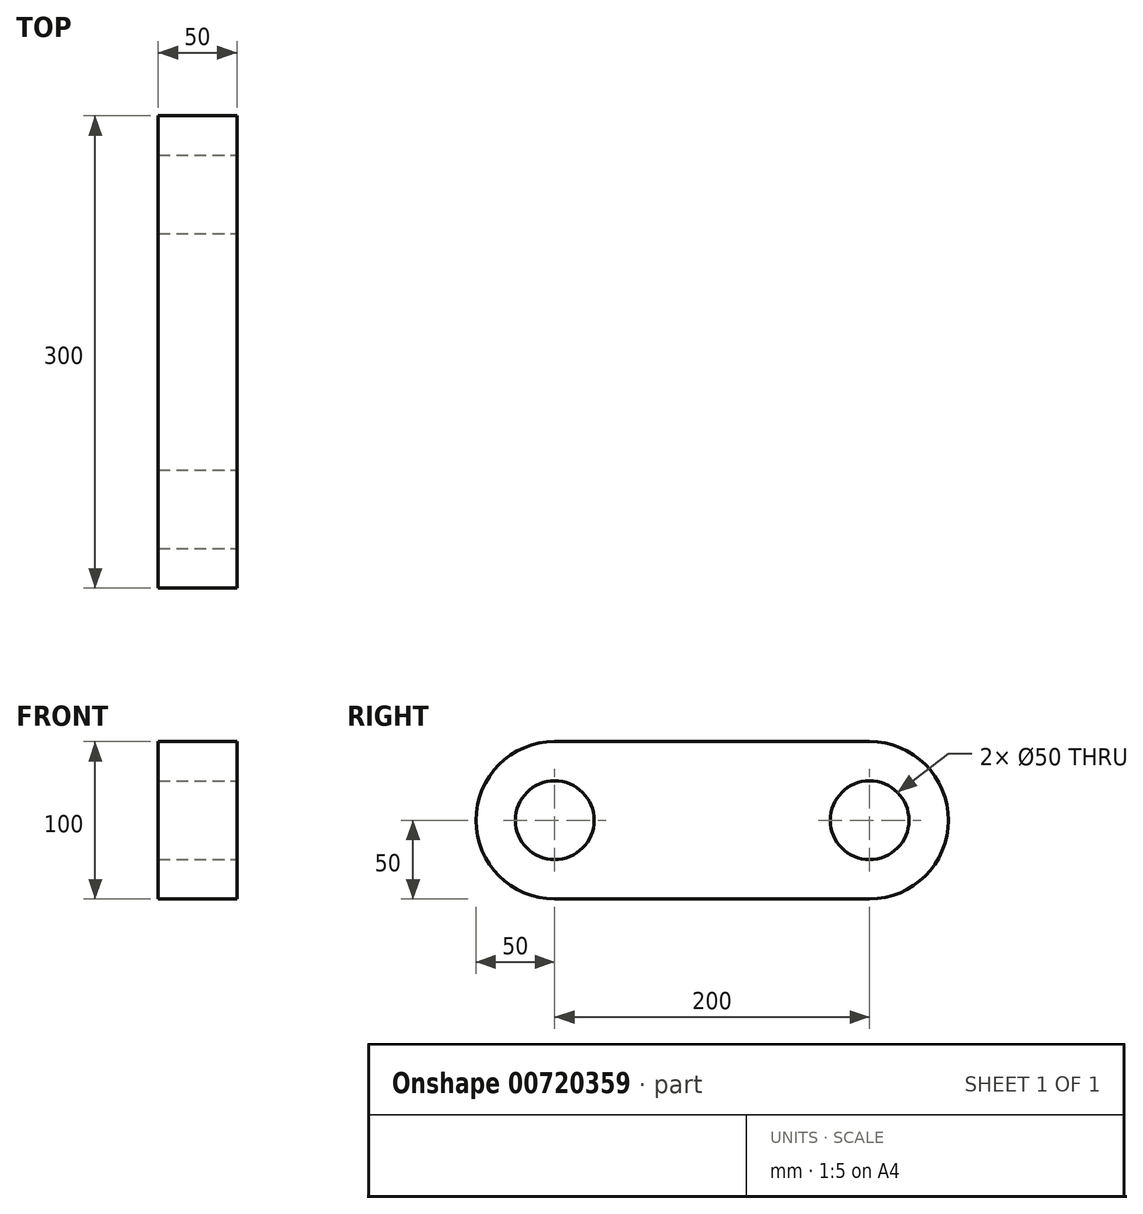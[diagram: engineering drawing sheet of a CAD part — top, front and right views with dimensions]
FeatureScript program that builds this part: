
annotation { "Feature Type Name" : "Feature", "Feature Type Description" : "" }
export const myFeature = defineFeature(function(context is Context, id is Id, definition is map)
    precondition{}
    {
        {
            var Q0;
            Q0=qCreatedBy(makeId("Right.planeOp"),FACE);
            var sketch = newSketch(context, id + "F0", { "sketchPlane" : qUnion([Q0])});
            skLineSegment(sketch, "E0.bottom", {"start": v(150, 50) * mm, "end": v(-150, 50) * mm});
            skLineSegment(sketch, "E0.top", {"start": v(150, -50) * mm, "end": v(-150, -50) * mm});
            skLineSegment(sketch, "E0.left", {"start": v(150, 50) * mm, "end": v(150, -50) * mm});
            skLineSegment(sketch, "E0.right", {"start": v(-150, 50) * mm, "end": v(-150, -50) * mm});
            skPoint(sketch, "E0.middle", {"position": v(0, 0) * mm});
            skSolve(sketch);
        }
        {
            var Q0;
            Q0=makeQuery(id+"F0.imprint","IMPRINT",FACE,{"disambiguationData":[TD([[makeQuery(id+"F0.imprint","IMPRINT",EDGE,{"derivedFrom":sQuery(id+"F0.wireOp",EDGE,"E0.bottom")}),1.0]])]});
            extrude(context, id + "F1", {"entities" : qUnion([Q0]), "depth" : 50 * mm, "offsetDistance" : 25 * mm});
        }
        {
            var Q0;
            Q0=makeQuery(id+"F1.opExtrude","SWEPT_EDGE",EDGE,{"disambiguationData":[OSD([sQuery(id+"F0.wireOp",EDGE,"E0.bottom"),sQuery(id+"F0.wireOp",EDGE,"E0.right")])]});
            var Q1;
            Q1=makeQuery(id+"F1.opExtrude","SWEPT_EDGE",EDGE,{"disambiguationData":[OSD([sQuery(id+"F0.wireOp",EDGE,"E0.top"),sQuery(id+"F0.wireOp",EDGE,"E0.right")])]});
            var Q2;
            Q2=makeQuery(id+"F1.opExtrude","SWEPT_EDGE",EDGE,{"disambiguationData":[OSD([sQuery(id+"F0.wireOp",EDGE,"E0.bottom"),sQuery(id+"F0.wireOp",EDGE,"E0.left")])]});
            var Q3;
            Q3=makeQuery(id+"F1.opExtrude","SWEPT_EDGE",EDGE,{"disambiguationData":[OSD([sQuery(id+"F0.wireOp",EDGE,"E0.top"),sQuery(id+"F0.wireOp",EDGE,"E0.left")])]});
            fillet(context, id + "F2", {"entities" : qUnion([Q0, Q1, Q2, Q3]), "radius" : 50 * mm, "tangentPropagation" : true, "allowEdgeOverflow" : false});
        }
        {
            var Q0;
            Q0=makeQuery(id+"F1.opExtrude","CAP_FACE",FACE,{"disambiguationData":[OSD([sQuery(id+"F0.wireOp",EDGE,"E0.bottom"),sQuery(id+"F0.wireOp",EDGE,"E0.top"),sQuery(id+"F0.wireOp",EDGE,"E0.left"),sQuery(id+"F0.wireOp",EDGE,"E0.right")])],"isStart":false});
            var sketch = newSketch(context, id + "F3", { "sketchPlane" : qUnion([Q0])});
            skCircle(sketch, "E1", {"center": v(-100, 0) * mm, "radius": 25 * mm});
            skCircle(sketch, "E2", {"center": v(100, 0) * mm, "radius": 25 * mm});
            skSolve(sketch);
        }
        {
            var Q0;
            Q0 = qSketchRegion(id + "F3", true);
            extrude(context, id + "F4", {"entities" : qUnion([Q0]), "operationType" : NewBodyOperationType.REMOVE, "oppositeDirection" : true, "depth" : 50 * mm, "offsetDistance" : 25 * mm});
        }
    });
